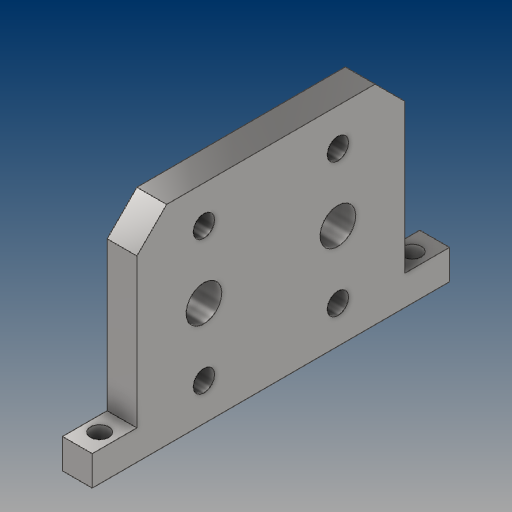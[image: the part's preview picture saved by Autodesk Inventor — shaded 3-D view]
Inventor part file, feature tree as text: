
AUTODESK INVENTOR PART (.ipt)
format: ipt  version: 2021 (Build 250183000, 183)  size: 179,712 bytes
history: native  units: mm
features: projected_geometry x5, sketch x4, extrude x2, hole x2, chamfer x1
ambient origin geometry x8: Origin, YZ Plane, XZ Plane, XY Plane, X Axis, Y Axis, Z Axis, Center Point
bodies: Solid1 (feature_tree)
feature tree (14):
  extrude  "Extrusion1"  Depth=120.0mm
  extrude  "Extrusion2"  Depth=52.0mm
  hole  "Hole1"  [1 undecoded]
  hole  "Hole2"  [1 undecoded]
  chamfer  "Chamfer1"  Distance=12.0mm
  sketch  "Sketch1"  dims[d0=35.0mm d1=120.0mm]
  sketch  "Sketch2"  dims[d2=45.0mm d3=52.0mm]
  projected_geometry  "Projected Loop1"
  projected_geometry  "Projected Loop2"
  sketch  "Sketch3"  dims[d4=36.0mm d5=75.0mm]
  projected_geometry  "Projected Loop3"
  sketch  "Sketch4"  dims[d6=15.0mm d7=9.0mm d8=12.0mm d9=12.0mm d10=10.0mm d11=0.0mm d14=60.0mm d15=0.0mm d16=45.0mm d17=7.2mm d18=6.0mm d19=4.0mm d20=2.0mm d21=90.0deg d22=8.0mm d23=20.594885mm d24=7.5mm d26=6.2mm d27=6.0mm d28=4.0mm d29=2.0mm d30=90.0deg d31=8.0mm d32=20.594885mm d33=10.0mm d34=2.0mm d35=45.0deg d36=15.0mm d37=15.0mm d38=7.5mm]
  projected_geometry  "Projected Loop4"
  projected_geometry  "Projected Loop5"
note: 2 required parameter values undecoded (feature->parameter linkage not recoverable at this tier; creation-order binding heuristic only, values carry confidence <= 0.55)
